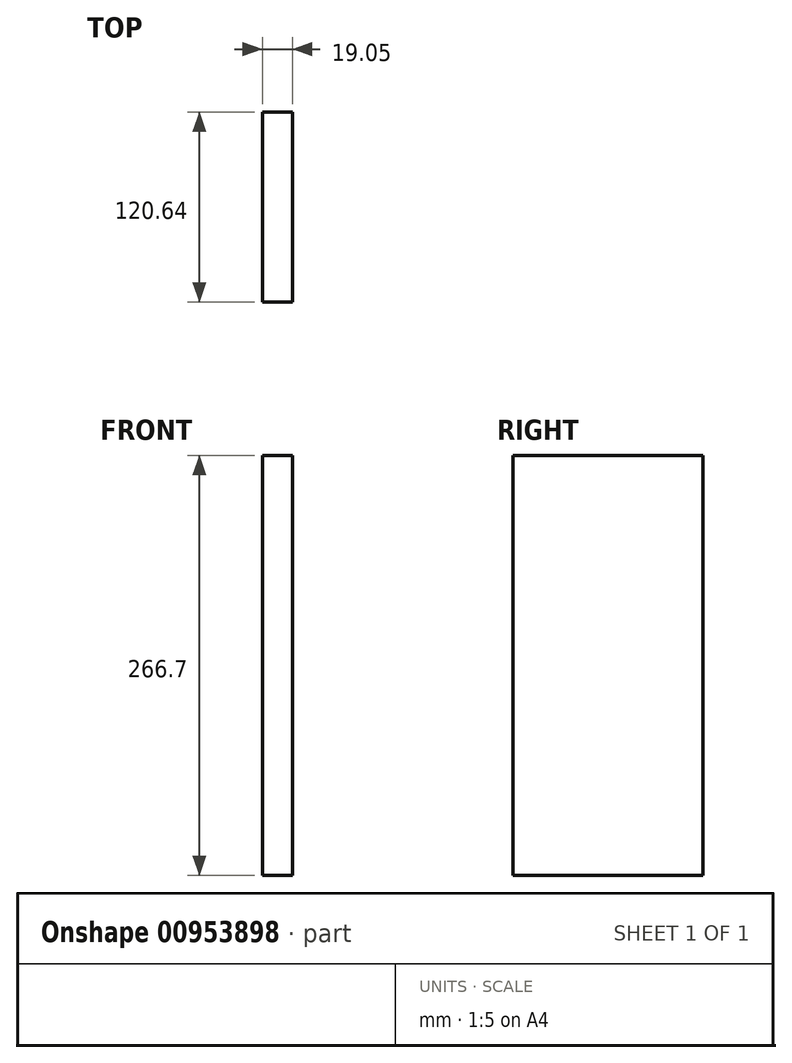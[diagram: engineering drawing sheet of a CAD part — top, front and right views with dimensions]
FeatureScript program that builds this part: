
annotation { "Feature Type Name" : "Feature", "Feature Type Description" : "" }
export const myFeature = defineFeature(function(context is Context, id is Id, definition is map)
    precondition{}
    {
        {
            var Q0;
            Q0=qCreatedBy(makeId("Right.planeOp"),FACE);
            var sketch = newSketch(context, id + "F0", { "sketchPlane" : qUnion([Q0])});
            skLineSegment(sketch, "E0.bottom", {"start": v(60.33, 133.35) * mm, "end": v(-60.33, 133.35) * mm});
            skLineSegment(sketch, "E0.top", {"start": v(60.33, -133.35) * mm, "end": v(-60.33, -133.35) * mm});
            skLineSegment(sketch, "E0.left", {"start": v(60.33, 133.35) * mm, "end": v(60.33, -133.35) * mm});
            skLineSegment(sketch, "E0.right", {"start": v(-60.33, 133.35) * mm, "end": v(-60.33, -133.35) * mm});
            skPoint(sketch, "E0.middle", {"position": v(0, 0) * mm});
            skSolve(sketch);
        }
        {
            var Q0;
            Q0 = qSketchRegion(id + "F0", true);
            extrude(context, id + "F1", {"entities" : qUnion([Q0]), "depth" : 19.05 * mm, "offsetDistance" : 25.4 * mm});
        }
    });
